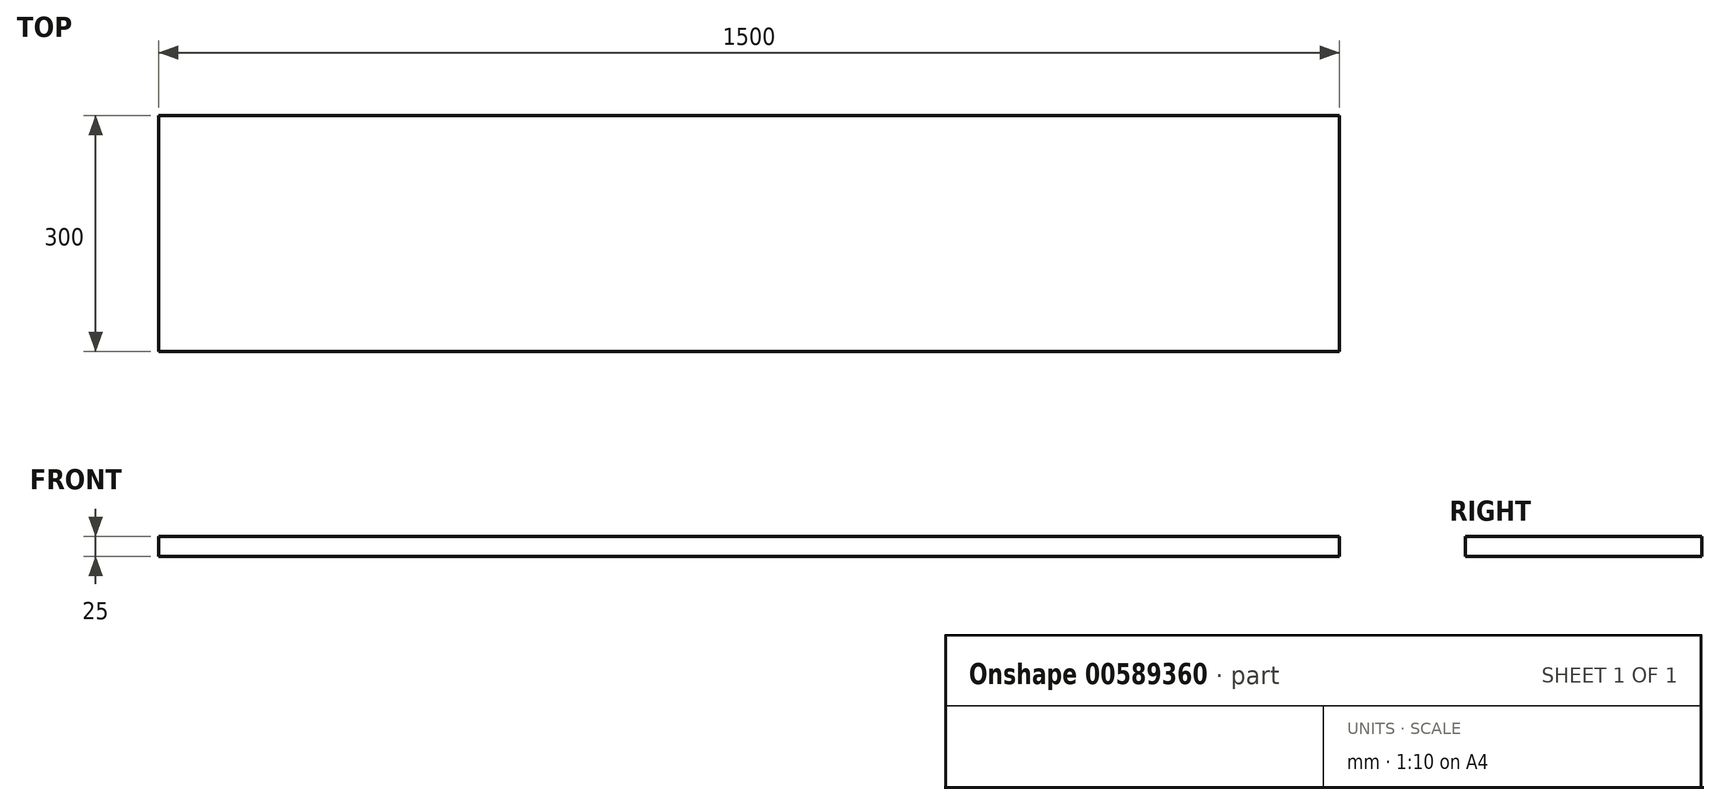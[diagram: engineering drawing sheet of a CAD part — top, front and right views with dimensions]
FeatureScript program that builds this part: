
annotation { "Feature Type Name" : "Feature", "Feature Type Description" : "" }
export const myFeature = defineFeature(function(context is Context, id is Id, definition is map)
    precondition{}
    {
        {
            var Q0;
            Q0=qCreatedBy(makeId("Top.planeOp"),FACE);
            var sketch = newSketch(context, id + "F0", { "sketchPlane" : qUnion([Q0])});
            skLineSegment(sketch, "E0.bottom", {"start": v(-750, 150) * mm, "end": v(750, 150) * mm});
            skLineSegment(sketch, "E0.top", {"start": v(-750, -150) * mm, "end": v(750, -150) * mm});
            skLineSegment(sketch, "E0.left", {"start": v(-750, 150) * mm, "end": v(-750, -150) * mm});
            skLineSegment(sketch, "E0.right", {"start": v(750, 150) * mm, "end": v(750, -150) * mm});
            skSolve(sketch);
        }
        {
            var Q0;
            Q0=makeQuery(id+"F0.imprint","IMPRINT",FACE,{"disambiguationData":[TD([[makeQuery(id+"F0.imprint","IMPRINT",EDGE,{"derivedFrom":sQuery(id+"F0.wireOp",EDGE,"E0.bottom")}),-1.0]])]});
            extrude(context, id + "F1", {"entities" : qUnion([Q0]), "depth" : 25 * mm, "offsetDistance" : 25 * mm});
        }
    });
